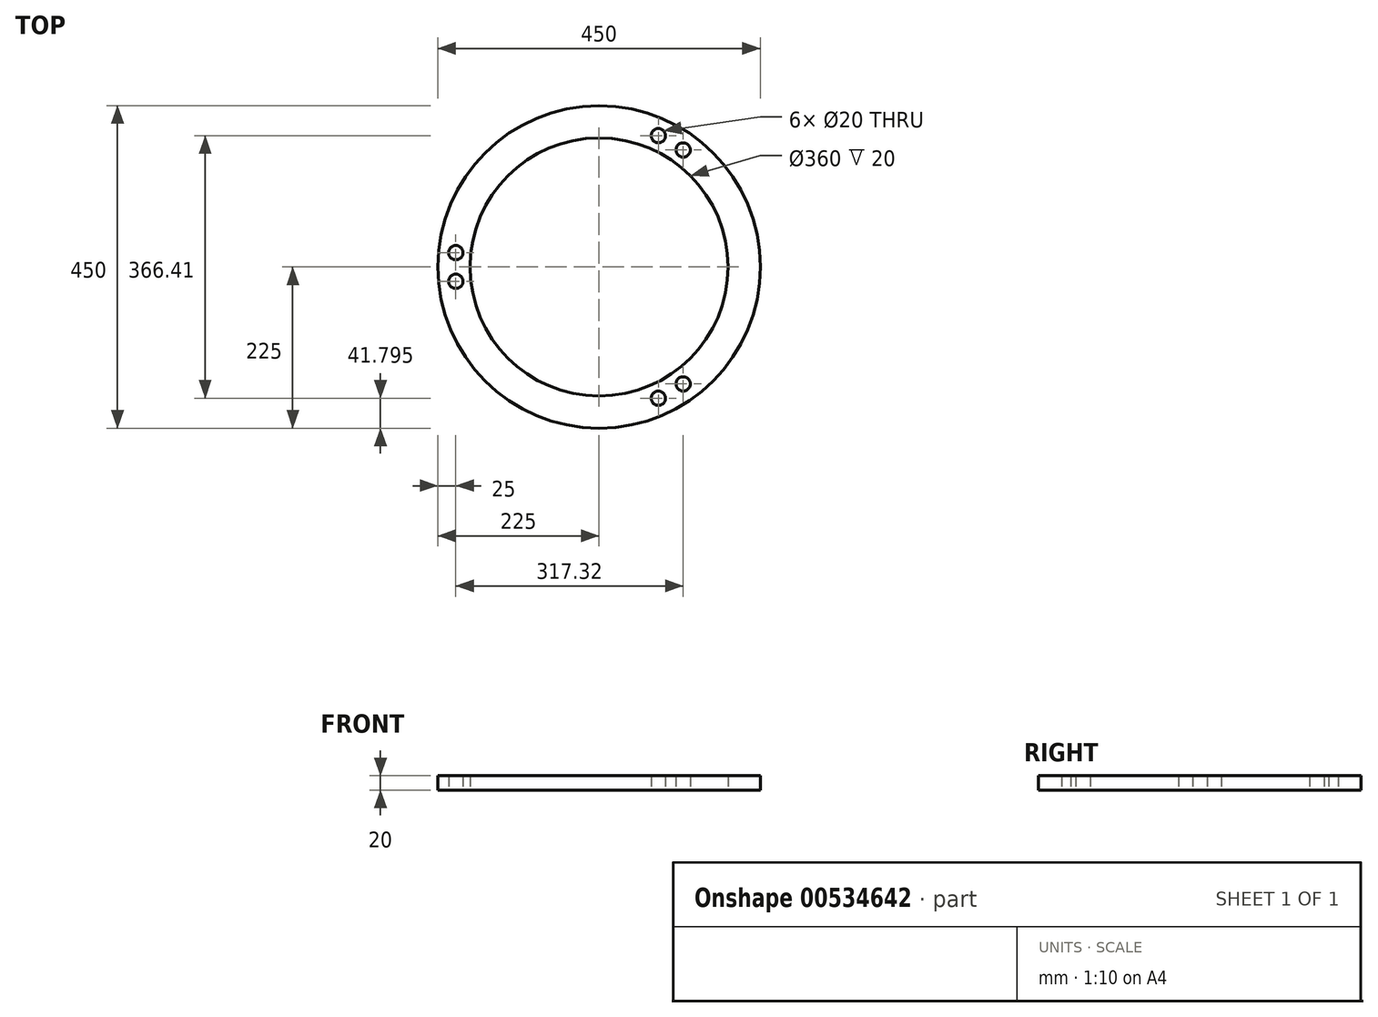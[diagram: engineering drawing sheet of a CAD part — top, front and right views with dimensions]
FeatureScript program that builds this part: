
annotation { "Feature Type Name" : "Feature", "Feature Type Description" : "" }
export const myFeature = defineFeature(function(context is Context, id is Id, definition is map)
    precondition{}
    {
        {
            var Q0;
            Q0=qCreatedBy(makeId("Top.planeOp"),FACE);
            var sketch = newSketch(context, id + "F0", { "sketchPlane" : qUnion([Q0])});
            skCircle(sketch, "E0", {"center": v(0, 0) * mm, "radius": 225 * mm});
            skLineSegment(sketch, "E1", {"start": v(0, 0) * mm, "end": v(-225, 0) * mm, "construction": true});
            skLineSegment(sketch, "E2", {"start": v(0, 0) * mm, "end": v(112.5, -194.86) * mm, "construction": true});
            skLineSegment(sketch, "E3", {"start": v(0, 0) * mm, "end": v(112.5, 194.86) * mm, "construction": true});
            skCircle(sketch, "E4", {"center": v(-200, 20) * mm, "radius": 10 * mm});
            skCircle(sketch, "E5", {"center": v(-200, -20) * mm, "radius": 10 * mm});
            skCircle(sketch, "E6", {"center": v(82.68, 183.2) * mm, "radius": 10 * mm});
            skCircle(sketch, "E7", {"center": v(117.32, 163.2) * mm, "radius": 10 * mm});
            skCircle(sketch, "E8", {"center": v(117.32, -163.2) * mm, "radius": 10 * mm});
            skCircle(sketch, "E9", {"center": v(82.68, -183.2) * mm, "radius": 10 * mm});
            skLineSegment(sketch, "E10", {"start": v(-200, 20) * mm, "end": v(-200, -20) * mm, "construction": true});
            skLineSegment(sketch, "E11", {"start": v(82.68, 183.2) * mm, "end": v(117.32, 163.2) * mm, "construction": true});
            skLineSegment(sketch, "E12", {"start": v(117.32, -163.2) * mm, "end": v(82.68, -183.2) * mm, "construction": true});
            skLineSegment(sketch, "E13", {"start": v(-200, 0) * mm, "end": v(0, 0) * mm, "construction": true});
            skLineSegment(sketch, "E14", {"start": v(100, 173.2) * mm, "end": v(0, 0) * mm, "construction": true});
            skLineSegment(sketch, "E15", {"start": v(100, -173.2) * mm, "end": v(0, 0) * mm, "construction": true});
            skCircle(sketch, "E16", {"center": v(0, 0) * mm, "radius": 180 * mm});
            skSolve(sketch);
        }
        {
            var Q0;
            Q0 = qSketchRegion(id + "F0", true);
            extrude(context, id + "F1", {"entities" : qUnion([Q0]), "depth" : 20 * mm, "offsetDistance" : 25 * mm});
        }
    });
